FCSTD DOCUMENT  (FreeCAD 1.0R39319 (Git))
Label: PcbBoard
License: All rights reserved
LicenseURL: http://en.wikipedia.org/wiki/All_rights_reserved
objects: Sketcher::SketchObject×1, PartDesign::Body×1
note: 3 computed .brp shape members not serialized (recipe doc carries the construction recipe); baked Part::Feature solids carry a one-line shape summary decoded from their .brp

FEATURE [Sketcher::SketchObject] Sketch
  ArcFitTolerance = 0
  AttachmentSupport = -> [XY_Plane]
  FullyConstrained = false
  MakeInternals = false
  MapMode = 5
  sketch-geometry (19):
    g0: LineSegment StartX=-28.65 StartY=-2.33827 StartZ=0 EndX=-16.365 EndY=-23.6165 EndZ=0
    g1: LineSegment StartX=-12.27 StartY=-25.9808 StartZ=0 EndX=12.273 EndY=-25.9808 EndZ=0
    g2: LineSegment StartX=16.3635 StartY=-23.6191 StartZ=0 EndX=28.635 EndY=-2.36425 EndZ=0
    g3: LineSegment StartX=28.635 StartY=2.36425 StartZ=0 EndX=16.35 EndY=23.6425 EndZ=0
    g4: LineSegment StartX=12.3 StartY=25.9808 StartZ=0 EndX=-12 EndY=25.9808 EndZ=0
    g5: LineSegment StartX=-16.5 StartY=23.3827 StartZ=0 EndX=-28.65 EndY=2.33827 EndZ=0
    g6: Circle [constr] CenterX=0 CenterY=0 CenterZ=0 NormalX=0 NormalY=0 NormalZ=1 AngleXU=0 Radius=30
    g7: ArcOfCircle CenterX=-12 CenterY=20.7846 CenterZ=0 NormalX=0 NormalY=0 NormalZ=1 AngleXU=0 Radius=5.19615 StartAngle=1.5708 EndAngle=2.61799
    g8: GeomPoint [constr] X=-15 Y=25.9808 Z=0
    g9: ArcOfCircle CenterX=12.3 CenterY=21.3042 CenterZ=0 NormalX=0 NormalY=0 NormalZ=1 AngleXU=0 Radius=4.67654 StartAngle=0.523599 EndAngle=1.5708
    g10: GeomPoint [constr] X=15 Y=25.9808 Z=0
    g11: ArcOfCircle CenterX=24.54 CenterY=-4e-15 CenterZ=0 NormalX=0 NormalY=0 NormalZ=1 AngleXU=0 Radius=4.7285 StartAngle=5.75959 EndAngle=6.80678
    g12: GeomPoint [constr] X=30 Y=-1.09e-14 Z=0
    g13: ArcOfCircle CenterX=-24.6 CenterY=3.7e-15 CenterZ=0 NormalX=0 NormalY=0 NormalZ=1 AngleXU=0 Radius=4.67654 StartAngle=2.61799 EndAngle=3.66519
    g14: GeomPoint [constr] X=-30 Y=0 Z=0
    g15: ArcOfCircle CenterX=-12.27 CenterY=-21.2523 CenterZ=0 NormalX=0 NormalY=0 NormalZ=1 AngleXU=0 Radius=4.7285 StartAngle=3.66519 EndAngle=4.71239
    g16: GeomPoint [constr] X=-15 Y=-25.9808 Z=0
    g17: ArcOfCircle CenterX=12.273 CenterY=-21.2575 CenterZ=0 NormalX=0 NormalY=0 NormalZ=1 AngleXU=0 Radius=4.7233 StartAngle=4.71239 EndAngle=5.75959
    g18: GeomPoint [constr] X=15 Y=-25.9808 Z=0
  constraints (33):
    c: PointOnObject(g16,g6)
    c: PointOnObject(g18,g6)
    c: PointOnObject(g12,g6)
    c: PointOnObject(g10,g6)
    c: PointOnObject(g8,g6)
    c: PointOnObject(g14,g6)
    c: Coincident(g6,g-1)
    c: Radius(g6) = 30
    c: PointOnObject(g14,g-1)
    c: PointOnObject(g8,g4)
    c: PointOnObject(g8,g5)
    c: Tangent(g4,g7) = -1.5708
    c: Tangent(g5,g7) = -1.5708
    c: PointOnObject(g10,g3)
    c: PointOnObject(g10,g4)
    c: Tangent(g3,g9) = -1.5708
    c: Tangent(g4,g9) = -1.5708
    c: PointOnObject(g12,g2)
    c: PointOnObject(g12,g3)
    c: Tangent(g2,g11) = -1.5708
    c: Tangent(g3,g11) = -1.5708
    c: PointOnObject(g14,g0)
    c: PointOnObject(g14,g5)
    c: Tangent(g0,g13) = -1.5708
    c: Tangent(g5,g13) = -1.5708
    c: PointOnObject(g16,g0)
    c: PointOnObject(g16,g1)
    c: Tangent(g0,g15) = -1.5708
    c: Tangent(g1,g15) = -1.5708
    c: PointOnObject(g18,g1)
    c: PointOnObject(g18,g2)
    c: Tangent(g1,g17) = -1.5708
    c: Tangent(g2,g17) = -1.5708
FEATURE [PartDesign::Body] Body
  AllowCompound = false
  Group = -> [Sketch]
  Origin = -> Origin
